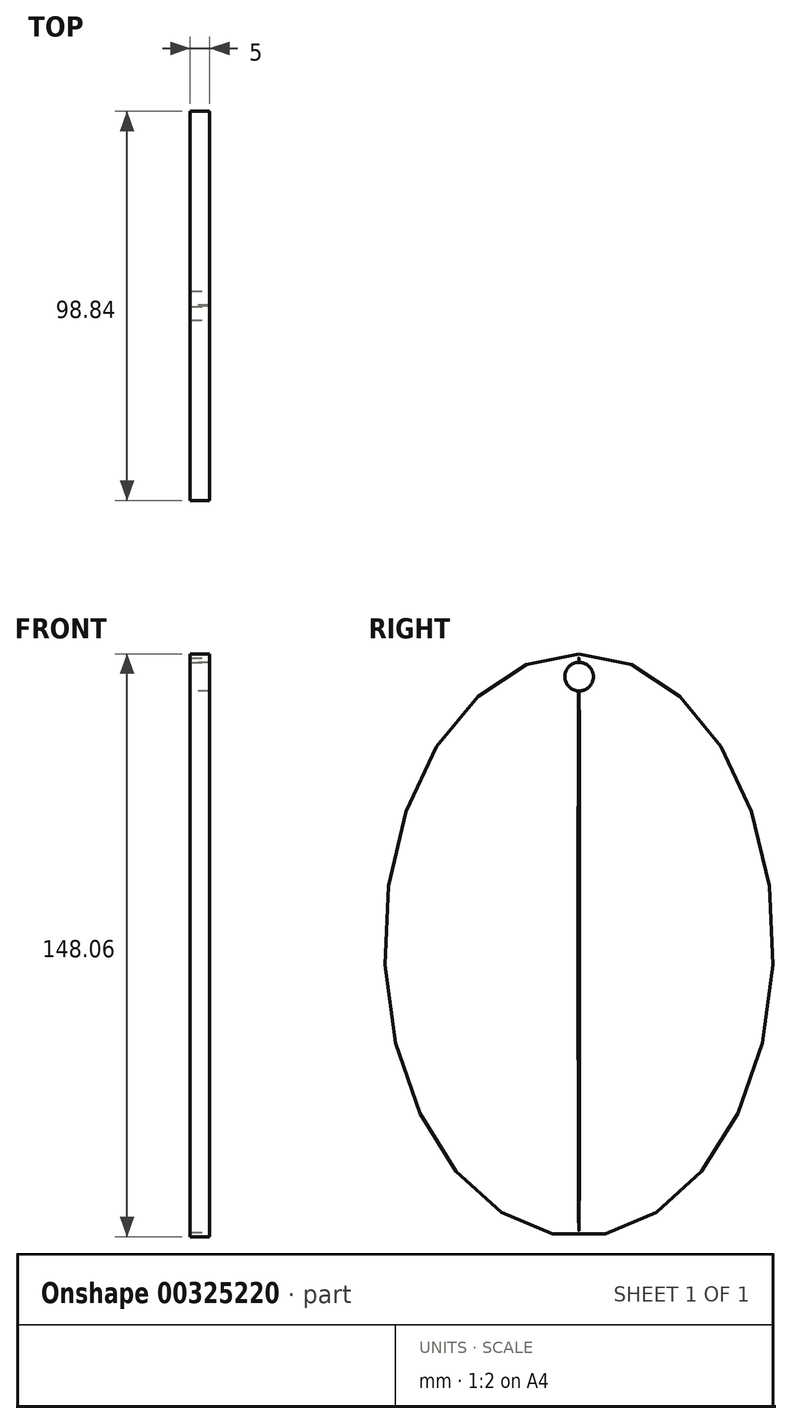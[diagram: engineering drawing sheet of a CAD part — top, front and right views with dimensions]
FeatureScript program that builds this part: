
annotation { "Feature Type Name" : "Feature", "Feature Type Description" : "" }
export const myFeature = defineFeature(function(context is Context, id is Id, definition is map)
    precondition{}
    {
        {
            var Q0;
            Q0=qCreatedBy(makeId("Right.planeOp"),FACE);
            var sketch = newSketch(context, id + "F0", { "sketchPlane" : qUnion([Q0])});
            skEllipse(sketch, "E0", {"center": v(0, 0) * mm, "majorRadius": 73 * mm, "minorRadius": 0.18 * mm, "majorAxis": v(0, 1)});
            skEllipse(sketch, "E1", {"center": v(0, 0) * mm, "majorRadius": 74.03 * mm, "minorRadius": 49.42 * mm, "majorAxis": v(0, 1)});
            skSolve(sketch);
        }
        {
            var Q0;
            Q0=makeQuery(id+"F0.imprint","IMPRINT",FACE,{"disambiguationData":[TD([[makeQuery(id+"F0.imprint","IMPRINT",EDGE,{"derivedFrom":sQuery(id+"F0.wireOp",EDGE,"E0")}),-1.0]])]});
            extrude(context, id + "F1", {"entities" : qUnion([Q0]), "depth" : 5 * mm});
        }
        {
            var Q0;
            Q0=makeQuery(id+"F1.opExtrude","CAP_FACE",FACE,{"disambiguationData":[OSD([sQuery(id+"F0.wireOp",EDGE,"E0"),sQuery(id+"F0.wireOp",EDGE,"E1")])],"isStart":false});
            var sketch = newSketch(context, id + "F2", { "sketchPlane" : qUnion([Q0])});
            skCircle(sketch, "E2", {"center": v(0.06, 68.25) * mm, "radius": 3.63 * mm});
            skSolve(sketch);
        }
        {
            var Q0;
            Q0 = qSketchRegion(id + "F2", true);
            extrude(context, id + "F3", {"entities" : qUnion([Q0]), "operationType" : NewBodyOperationType.REMOVE, "oppositeDirection" : true, "depth" : 5 * mm});
        }
    });
